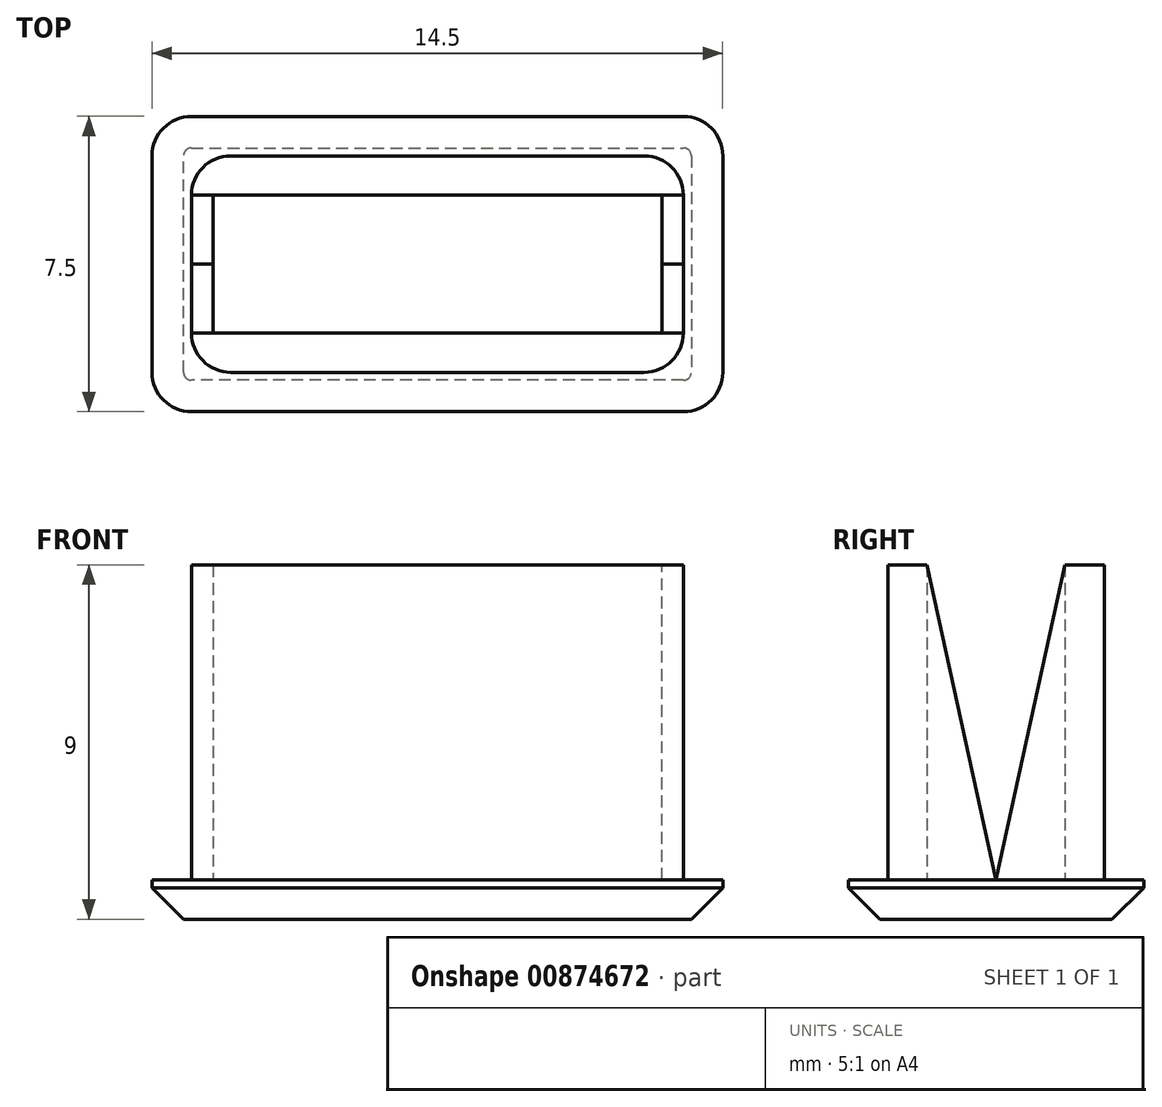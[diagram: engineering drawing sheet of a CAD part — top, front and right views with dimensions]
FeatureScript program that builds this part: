
annotation { "Feature Type Name" : "Feature", "Feature Type Description" : "" }
export const myFeature = defineFeature(function(context is Context, id is Id, definition is map)
    precondition{}
    {
        {
            var Q0;
            Q0=qCreatedBy(makeId("Top.planeOp"),FACE);
            var sketch = newSketch(context, id + "F0", { "sketchPlane" : qUnion([Q0])});
            skLineSegment(sketch, "E0.bottom", {"start": v(-18.1, 7.52) * mm, "end": v(-5.6, 7.52) * mm});
            skLineSegment(sketch, "E0.top", {"start": v(-18.1, 2.02) * mm, "end": v(-5.6, 2.02) * mm});
            skLineSegment(sketch, "E0.left", {"start": v(-18.1, 7.52) * mm, "end": v(-18.1, 2.02) * mm});
            skLineSegment(sketch, "E0.right", {"start": v(-5.6, 7.52) * mm, "end": v(-5.6, 2.02) * mm});
            skLineSegment(sketch, "E1.0", {"start": v(-19.1, 8.52) * mm, "end": v(-4.6, 8.52) * mm});
            skLineSegment(sketch, "E1.1", {"start": v(-19.1, 8.52) * mm, "end": v(-19.1, 1.02) * mm});
            skLineSegment(sketch, "E1.2", {"start": v(-19.1, 1.02) * mm, "end": v(-4.6, 1.02) * mm});
            skLineSegment(sketch, "E1.3", {"start": v(-4.6, 8.52) * mm, "end": v(-4.6, 1.02) * mm});
            skLineSegment(sketch, "E2", {"start": v(-6.16, 6.52) * mm, "end": v(-17.56, 6.52) * mm});
            skLineSegment(sketch, "E3", {"start": v(-17.56, 6.52) * mm, "end": v(-17.56, 3.02) * mm});
            skLineSegment(sketch, "E4", {"start": v(-17.56, 3.02) * mm, "end": v(-6.16, 3.02) * mm});
            skLineSegment(sketch, "E5", {"start": v(-6.16, 3.02) * mm, "end": v(-6.16, 6.52) * mm});
            skSolve(sketch);
        }
        {
            var Q0;
            Q0=makeQuery(id+"F0.imprint","IMPRINT",FACE,{"disambiguationData":[TD([[makeQuery(id+"F0.imprint","IMPRINT",EDGE,{"derivedFrom":sQuery(id+"F0.wireOp",EDGE,"E0.bottom")}),-1.0]])]});
            extrude(context, id + "F1", {"entities" : qUnion([Q0]), "depth" : 8 * mm, "offsetDistance" : 25 * mm});
        }
        {
            var Q0;
            Q0=makeQuery(id+"F0.imprint","IMPRINT",FACE,{"disambiguationData":[TD([[makeQuery(id+"F0.imprint","IMPRINT",EDGE,{"derivedFrom":sQuery(id+"F0.wireOp",EDGE,"E0.bottom")}),1.0]])]});
            var Q1;
            Q1=makeQuery(id+"F0.imprint","IMPRINT",FACE,{"disambiguationData":[TD([[makeQuery(id+"F0.imprint","IMPRINT",EDGE,{"derivedFrom":sQuery(id+"F0.wireOp",EDGE,"E2")}),1.0]])]});
            var Q2;
            Q2=makeQuery(id+"F0.imprint","IMPRINT",FACE,{"disambiguationData":[TD([[makeQuery(id+"F0.imprint","IMPRINT",EDGE,{"derivedFrom":sQuery(id+"F0.wireOp",EDGE,"E0.bottom")}),-1.0]])]});
            extrude(context, id + "F2", {"entities" : qUnion([Q0, Q1, Q2]), "operationType" : NewBodyOperationType.ADD, "oppositeDirection" : true, "depth" : 1 * mm, "offsetDistance" : 25 * mm});
        }
        {
            var Q0;
            Q0=makeQuery(id+"F1.opExtrude","SWEPT_EDGE",EDGE,{"disambiguationData":[OSD([sQuery(id+"F0.wireOp",EDGE,"E0.top"),sQuery(id+"F0.wireOp",EDGE,"E0.left")])]});
            var Q1;
            Q1=makeQuery(id+"F1.opExtrude","SWEPT_EDGE",EDGE,{"disambiguationData":[OSD([sQuery(id+"F0.wireOp",EDGE,"E0.top"),sQuery(id+"F0.wireOp",EDGE,"E0.right")])]});
            var Q2;
            Q2=makeQuery(id+"F1.opExtrude","SWEPT_EDGE",EDGE,{"disambiguationData":[OSD([sQuery(id+"F0.wireOp",EDGE,"E0.bottom"),sQuery(id+"F0.wireOp",EDGE,"E0.left")])]});
            var Q3;
            Q3=makeQuery(id+"F1.opExtrude","SWEPT_EDGE",EDGE,{"disambiguationData":[OSD([sQuery(id+"F0.wireOp",EDGE,"E0.bottom"),sQuery(id+"F0.wireOp",EDGE,"E0.right")])]});
            var Q4;
            Q4=makeQuery(id+"F2.opExtrude","SWEPT_EDGE",EDGE,{"disambiguationData":[OSD([sQuery(id+"F0.wireOp",EDGE,"E1.1"),sQuery(id+"F0.wireOp",EDGE,"E1.2")])]});
            var Q5;
            Q5=makeQuery(id+"F2.opExtrude","SWEPT_EDGE",EDGE,{"disambiguationData":[OSD([sQuery(id+"F0.wireOp",EDGE,"E1.2"),sQuery(id+"F0.wireOp",EDGE,"E1.3")])]});
            var Q6;
            Q6=makeQuery(id+"F2.opExtrude","SWEPT_EDGE",EDGE,{"disambiguationData":[OSD([sQuery(id+"F0.wireOp",EDGE,"E1.0"),sQuery(id+"F0.wireOp",EDGE,"E1.1")])]});
            var Q7;
            Q7=makeQuery(id+"F2.opExtrude","SWEPT_EDGE",EDGE,{"disambiguationData":[OSD([sQuery(id+"F0.wireOp",EDGE,"E1.0"),sQuery(id+"F0.wireOp",EDGE,"E1.3")])]});
            fillet(context, id + "F3", {"entities" : qUnion([Q0, Q1, Q2, Q3, Q4, Q5, Q6, Q7]), "radius" : 1 * mm, "tangentPropagation" : true, "allowEdgeOverflow" : false});
        }
        {
            var Q0;
            Q0=makeQuery(id+"F1.opExtrude","SWEPT_FACE",FACE,{"disambiguationData":[OSD([sQuery(id+"F0.wireOp",EDGE,"E0.right")])]});
            var sketch = newSketch(context, id + "F4", { "sketchPlane" : qUnion([Q0])});
            skLineSegment(sketch, "E6", {"start": v(3.02, 8) * mm, "end": v(4.77, 0) * mm});
            skLineSegment(sketch, "E7", {"start": v(4.77, 0) * mm, "end": v(6.52, 8) * mm});
            skSolve(sketch);
        }
        {
            var Q0;
            Q0=makeQuery(id+"F4.imprint","IMPRINT",FACE,{"disambiguationData":[TD([[makeQuery(id+"F4.imprint","IMPRINT",EDGE,{"derivedFrom":sQuery(id+"F4.wireOp",EDGE,"E6")}),1.0]])]});
            extrude(context, id + "F5", {"entities" : qUnion([Q0]), "operationType" : NewBodyOperationType.REMOVE, "oppositeDirection" : true, "depth" : 25 * mm, "offsetDistance" : 25 * mm});
        }
        {
            var Q0;
            Q0=makeQuery(id+"F2.opExtrude","CAP_EDGE",EDGE,{"disambiguationData":[OSD([sQuery(id+"F0.wireOp",EDGE,"E1.2")])],"isStart":false});
            var Q1;
            {var subQ0=sQuery(id+"F0.wireOp",EDGE,"E1.2");var subQ1=sQuery(id+"F0.wireOp",EDGE,"E1.1");Q1=makeQuery(id+"F3.opFillet","BLEND_EDGE",EDGE,{"blendedFrom":[makeQuery(id+"F2.opExtrude","SWEPT_EDGE",EDGE,{"disambiguationData":[OSD([subQ1,subQ0])]}),makeQuery(id+"F2.opExtrude","CAP_FACE",FACE,{"disambiguationData":[OSD([sQuery(id+"F0.wireOp",EDGE,"E1.0"),subQ1,subQ0,sQuery(id+"F0.wireOp",EDGE,"E1.3")])],"isStart":false})],"blendedInto":[makeQuery(id+"F2.opExtrude","CAP_FACE",FACE,{"disambiguationData":[OSD([sQuery(id+"F0.wireOp",EDGE,"E1.0"),subQ1,subQ0,sQuery(id+"F0.wireOp",EDGE,"E1.3")])],"isStart":false})]});}
            var Q2;
            {var subQ0=sQuery(id+"F0.wireOp",EDGE,"E1.3");var subQ1=sQuery(id+"F0.wireOp",EDGE,"E1.2");Q2=makeQuery(id+"F3.opFillet","BLEND_EDGE",EDGE,{"blendedFrom":[makeQuery(id+"F2.opExtrude","SWEPT_EDGE",EDGE,{"disambiguationData":[OSD([subQ1,subQ0])]}),makeQuery(id+"F2.opExtrude","CAP_FACE",FACE,{"disambiguationData":[OSD([sQuery(id+"F0.wireOp",EDGE,"E1.0"),sQuery(id+"F0.wireOp",EDGE,"E1.1"),subQ1,subQ0])],"isStart":false})],"blendedInto":[makeQuery(id+"F2.opExtrude","CAP_FACE",FACE,{"disambiguationData":[OSD([sQuery(id+"F0.wireOp",EDGE,"E1.0"),sQuery(id+"F0.wireOp",EDGE,"E1.1"),subQ1,subQ0])],"isStart":false})]});}
            var Q3;
            Q3=makeQuery(id+"F2.opExtrude","CAP_EDGE",EDGE,{"disambiguationData":[OSD([sQuery(id+"F0.wireOp",EDGE,"E1.3")])],"isStart":false});
            var Q4;
            {var subQ0=sQuery(id+"F0.wireOp",EDGE,"E1.3");var subQ1=sQuery(id+"F0.wireOp",EDGE,"E1.0");Q4=makeQuery(id+"F3.opFillet","BLEND_EDGE",EDGE,{"blendedFrom":[makeQuery(id+"F2.opExtrude","SWEPT_EDGE",EDGE,{"disambiguationData":[OSD([subQ1,subQ0])]}),makeQuery(id+"F2.opExtrude","CAP_FACE",FACE,{"disambiguationData":[OSD([subQ1,sQuery(id+"F0.wireOp",EDGE,"E1.1"),sQuery(id+"F0.wireOp",EDGE,"E1.2"),subQ0])],"isStart":false})],"blendedInto":[makeQuery(id+"F2.opExtrude","CAP_FACE",FACE,{"disambiguationData":[OSD([subQ1,sQuery(id+"F0.wireOp",EDGE,"E1.1"),sQuery(id+"F0.wireOp",EDGE,"E1.2"),subQ0])],"isStart":false})]});}
            var Q5;
            Q5=makeQuery(id+"F2.opExtrude","CAP_EDGE",EDGE,{"disambiguationData":[OSD([sQuery(id+"F0.wireOp",EDGE,"E1.0")])],"isStart":false});
            var Q6;
            Q6=makeQuery(id+"F2.opExtrude","CAP_EDGE",EDGE,{"disambiguationData":[OSD([sQuery(id+"F0.wireOp",EDGE,"E1.1")])],"isStart":false});
            var Q7;
            {var subQ0=sQuery(id+"F0.wireOp",EDGE,"E1.1");var subQ1=sQuery(id+"F0.wireOp",EDGE,"E1.0");Q7=makeQuery(id+"F3.opFillet","BLEND_EDGE",EDGE,{"blendedFrom":[makeQuery(id+"F2.opExtrude","SWEPT_EDGE",EDGE,{"disambiguationData":[OSD([subQ1,subQ0])]}),makeQuery(id+"F2.opExtrude","CAP_FACE",FACE,{"disambiguationData":[OSD([subQ1,subQ0,sQuery(id+"F0.wireOp",EDGE,"E1.2"),sQuery(id+"F0.wireOp",EDGE,"E1.3")])],"isStart":false})],"blendedInto":[makeQuery(id+"F2.opExtrude","CAP_FACE",FACE,{"disambiguationData":[OSD([subQ1,subQ0,sQuery(id+"F0.wireOp",EDGE,"E1.2"),sQuery(id+"F0.wireOp",EDGE,"E1.3")])],"isStart":false})]});}
            chamfer(context, id + "F6", {"entities" : qUnion([Q0, Q1, Q2, Q3, Q4, Q5, Q6, Q7]), "width" : 0.8 * mm, "tangentPropagation" : true});
        }
    });
